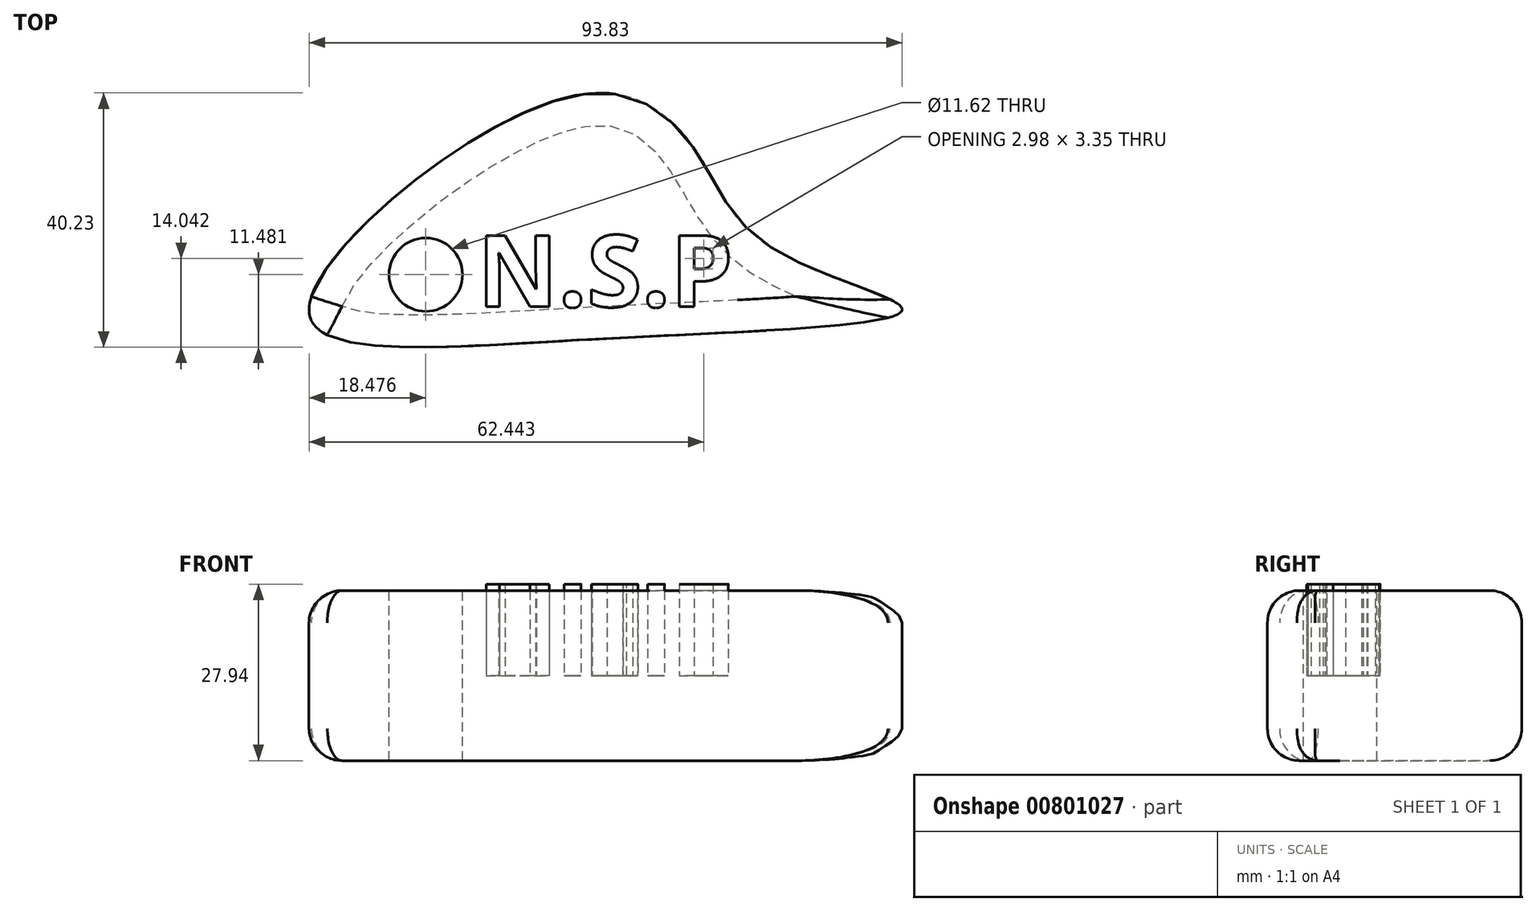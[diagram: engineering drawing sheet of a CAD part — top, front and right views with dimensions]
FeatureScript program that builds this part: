
annotation { "Feature Type Name" : "Feature", "Feature Type Description" : "" }
export const myFeature = defineFeature(function(context is Context, id is Id, definition is map)
    precondition{}
    {
        {
            var Q0;
            Q0=qCreatedBy(makeId("Top.planeOp"),FACE);
            var sketch = newSketch(context, id + "F0", { "sketchPlane" : qUnion([Q0])});
            skFitSpline(sketch, "E0", {"points": [v(0, 33.81) * mm, v(-42.54, 0) * mm, v(0, -4.98) * mm, v(51.28, 0) * mm, v(30.56, 9.65) * mm, v(19.2, 24.06) * mm, v(0, 33.81) * mm]});
            skSolve(sketch);
        }
        {
            var Q0;
            Q0 = qSketchRegion(id + "F0", true);
            extrude(context, id + "F1", {"entities" : qUnion([Q0]), "endBound" : BoundingType.SYMMETRIC, "depth" : 26.92 * mm, "offsetDistance" : 25.4 * mm});
        }
        {
            var Q0;
            Q0=qCreatedBy(makeId("Top.planeOp"),FACE);
            var sketch = newSketch(context, id + "F2", { "sketchPlane" : qUnion([Q0])});
            skCircle(sketch, "E1", {"center": v(-24.06, 5.38) * mm, "radius": 5.8 * mm});
            skSolve(sketch);
        }
        {
            var Q0;
            Q0 = qSketchRegion(id + "F2", true);
            extrude(context, id + "F3", {"entities" : qUnion([Q0]), "operationType" : NewBodyOperationType.REMOVE, "endBound" : BoundingType.SYMMETRIC, "oppositeDirection" : true, "depth" : 58.42 * mm, "offsetDistance" : 25.4 * mm});
        }
        {
            var Q0;
            Q0=qCreatedBy(makeId("Top.planeOp"),FACE);
            var sketch = newSketch(context, id + "F4", { "sketchPlane" : qUnion([Q0])});
            skText(sketch, "E2", { "text": "N.S.P", "fontName": "OpenSans-Bold.ttf"});
            const initialGuessF4  = {"E2": [-0.01594, 0.0003, 1, 0, 0.01137]};
            skSetInitialGuess(sketch, initialGuessF4);
            skSolve(sketch);
        }
        {
            var Q0;
            Q0 = qSketchRegion(id + "F4", true);
            extrude(context, id + "F5", {"entities" : qUnion([Q0]), "depth" : 14.48 * mm, "offsetDistance" : 25.4 * mm});
        }
        {
            var Q0;
            Q0=makeQuery(id+"F1.opExtrude","CAP_EDGE",EDGE,{"disambiguationData":[OSD([sQuery(id+"F0.wireOp",EDGE,"E0")])],"isStart":false});
            var Q1;
            Q1=makeQuery(id+"F1.opExtrude","SWEPT_FACE",FACE,{"disambiguationData":[OSD([sQuery(id+"F0.wireOp",EDGE,"E0")])]});
            fillet(context, id + "F6", {"entities" : qUnion([Q0, Q1]), "radius" : 5.08 * mm, "tangentPropagation" : true, "allowEdgeOverflow" : false});
        }
    });
